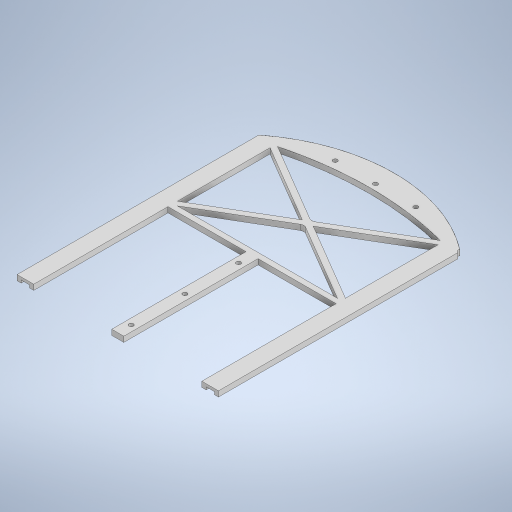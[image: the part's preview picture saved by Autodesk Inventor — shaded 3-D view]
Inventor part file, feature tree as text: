
AUTODESK INVENTOR PART (.ipt)
format: ipt  version: 2023 (Build 270158000, 158)  size: 345,600 bytes
history: native  units: mm
features: sketch x8, extrude x6, hole x2, other x1, fillet x1
ambient origin geometry x8: Origin, YZ Plane, XZ Plane, XY Plane, X Axis, Y Axis, Z Axis, Center Point
bodies: Body1 (feature_tree)
feature tree (18):
  other  "ソリッド1"
  extrude  "押し出し1"  Depth=150.0mm
  extrude  "押し出し2"  Depth=180.0mm
  extrude  "押し出し3"  Depth=4.0mm TaperAngle=0.0deg
  extrude  "押し出し4"  Depth=125.2mm
  extrude  "押し出し5"  Depth=100.0mm
  hole  "穴1"  [1 undecoded]
  extrude  "押し出し6"  Depth=4.0mm TaperAngle=0.0deg
  hole  "穴2"  [1 undecoded]
  fillet  "フィレット1"  Radius=180.0mm
  sketch  "スケッチ1"
  sketch  "スケッチ2"
  sketch  "スケッチ3"
  sketch  "スケッチ4"
  sketch  "スケッチ5"
  sketch  "スケッチ6"
  sketch  "スケッチ7"
  sketch  "スケッチ8"
note: 2 required parameter values undecoded (feature->parameter linkage not recoverable at this tier; creation-order binding heuristic only, values carry confidence <= 0.55)
